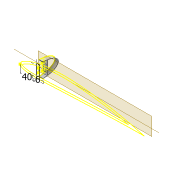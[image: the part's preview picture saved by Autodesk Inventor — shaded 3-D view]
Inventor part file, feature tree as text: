
AUTODESK INVENTOR PART (.ipt)
format: ipt  version: 2022 (Build 260153000, 153)  size: 1,056,256 bytes
history: native  units: mm
features: sketch x23, projected_geometry x15, extrude x12, plane x11, shell x2, chamfer x2, loft x1, fillet x1, other x1
ambient origin geometry x8: Origin, YZ Plane, XZ Plane, XY Plane, X Axis, Y Axis, Z Axis, Center Point
bodies: Solid1 (feature_tree)
feature tree (68):
  extrude  "Extrusion1"  Depth=5.0mm
  shell  "Shell1"  Thickness=6.0mm
  extrude  "Extrusion2"  Depth=2.0mm
  extrude  "Extrusion3"  Depth=5.9mm
  extrude  "Extrusion4"  Depth=10.0mm TaperAngle=0.0deg
  sketch  "Sketch29"  dims[d24=2.0mm d26=2.0mm d67=-30.0mm]
  plane  "Work Plane19"
  sketch  "Sketch28"  dims[d15=40.0mm d16=10.0mm d17=0.0mm]
  plane  "Work Plane20"
  sketch  "Sketch30"  dims[d68=-60.0mm d75=-90.0mm]
  plane  "Work Plane21"
  plane  "Work Plane22"
  plane  "Work Plane23"
  plane  "Work Plane24"
  plane  "Work Plane25"
  plane  "Work Plane26"
  plane  "Work Plane27"
  loft  "Loft7"
  extrude  "Extrusion11"  Depth=2.0mm
  shell  "Shell7"  Thickness=-30.0mm
  extrude  "Extrusion12"  [1 undecoded]
  plane  "Work Plane28"
  sketch  "Sketch45"  dims[d112=-250.0mm]
  extrude  "Extrusion13"  [1 undecoded]
  extrude  "Extrusion14"  [1 undecoded]
  extrude  "Extrusion15"  Depth=40.0mm
  extrude  "Extrusion16"  Depth=32.0mm
  extrude  "Extrusion17"  Depth=24.0mm
  chamfer  "Chamfer1"  Angle=90.0deg  [1 undecoded]
  chamfer  "Chamfer2"  Angle=90.0deg  [1 undecoded]
  fillet  "Fillet1"  [1 undecoded]
  sketch  "Sketch49"  dims[d171=0.0mm d172=90.0deg d173=0.0mm d174=90.0deg]
  plane  "Work Plane29"
  sketch  "Sketch51"  dims[d177=0.0mm d178=90.0deg d179=0.0mm d180=90.0deg d181=0.0mm d182=90.0deg d183=0.0mm d184=90.0deg d185=1000.0mm d186=0.0mm d187=1.0mm d188=1000.0mm d189=0.0mm d190=-11.0mm d191=1.0mm d192=0.0mm d193=1.0mm d194=0.0mm d195=2.1mm d196=2.1mm d197=5.9mm d198=12.0mm d199=2.8mm d200=2.8mm d201=3.0mm d202=0.0mm d203=4.0mm d204=4.0mm d205=4.0mm d206=1.25mm d207=3.25mm d208=0.0mm d209=0.0mm d210=2.0mm d211=0.0mm d212=40.0mm d213=2.0mm d214=45.0deg d215=40.0mm d216=2.0mm d217=45.0deg d218=2.0mm d219=240.0mm d220=0.0mm d222=2.95mm]
  other  "Work Axis1"
  extrude  "Extrusion18"  TaperAngle=0.0deg  [1 undecoded]
  sketch  "Sketch3"  dims[d0=4.5mm d1=0.0mm d2=5.0mm d3=6.0mm]
  sketch  "Sketch7"  dims[d5=4.5mm d6=0.0mm d7=2.0mm]
  projected_geometry  "Projected Loop3"
  sketch  "Sketch8"  dims[d8=2.0mm d9=5.9mm]
  sketch  "Sketch9"  dims[d12=4.0mm d13=10.0mm d14=0.0mm]
  sketch  "Sketch31"  dims[d76=-120.0mm d77=-150.0mm]
  sketch  "Sketch33"  dims[d78=-180.0mm d79=-210.0mm]
  sketch  "Sketch34"  dims[d80=-240.0mm d81=40.0mm]
  sketch  "Sketch35"  dims[d82=36.0mm d83=32.0mm]
  sketch  "Sketch36"  dims[d84=28.0mm d85=24.0mm]
  sketch  "Sketch37"  dims[d86=20.0mm]
  sketch  "Sketch40"  dims[d87=17.0mm]
  sketch  "Sketch43"  dims[d88=14.0mm]
  sketch  "Sketch44"  dims[d89=11.0mm]
  sketch  "Sketch46"  dims[d135=10.0mm]
  sketch  "Sketch47"  dims[d163=18.0mm]
  sketch  "Sketch48"  dims[d164=18.0mm d165=0.0mm d166=90.0deg d167=0.0mm d168=90.0deg d169=0.0mm d170=90.0deg]
  projected_geometry  "Projected Loop8"
  sketch  "Sketch50"  dims[d175=0.0mm d176=90.0deg]
  projected_geometry  "Project Cut Edges13"
  projected_geometry  "Project Cut Edges14"
  projected_geometry  "Project Cut Edges15"
  projected_geometry  "Project Cut Edges16"
  projected_geometry  "Project Cut Edges17"
  projected_geometry  "Project Cut Edges18"
  projected_geometry  "Project Cut Edges19"
  projected_geometry  "Project Cut Edges20"
  projected_geometry  "Project Cut Edges21"
  projected_geometry  "Project Cut Edges23"
  projected_geometry  "Project Cut Edges24"
  projected_geometry  "Project Cut Edges25"
  projected_geometry  "Project Cut Edges26"
note: 7 required parameter values undecoded (feature->parameter linkage not recoverable at this tier; creation-order binding heuristic only, values carry confidence <= 0.55)
